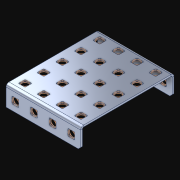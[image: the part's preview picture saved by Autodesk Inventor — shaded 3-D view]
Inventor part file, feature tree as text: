
AUTODESK INVENTOR PART (.ipt)
format: ipt  version: 2021 (Build 250183000, 183)  size: 1,430,528 bytes
history: native  units: in
note: dims shown in document units (in); Inventor stores cm internally (conversion verified against a paired STEP export)
features: extrude x29, other x29, sketch x4, pattern_linear x3
ambient origin geometry x8: Origin, YZ Plane, XZ Plane, XY Plane, X Axis, Y Axis, Z Axis, Center Point
bodies: Solid1 (feature_tree)
feature tree (65):
  pattern_linear  "Rectangular Pattern1"  Spacing1=0.182in  [1 undecoded]
  pattern_linear  "Rectangular Pattern2"  Spacing1=0.046in  [1 undecoded]
  pattern_linear  "Rectangular Pattern3"  Spacing1=0.5in  [1 undecoded]
  extrude  "Extrusion1"  Depth=0.5in
  sketch  "Sketch1"  dims[d0=0.182in]
  other  "Srf1"
  sketch  "Sketch2"  dims[d1=0.046in d2=0.0in]
  other  "Srf2"
  sketch  "Sketch3"  dims[d3=0.182in]
  other  "Srf3"
  other  "Srf4"
  other  "Srf5"
  other  "Srf6"
  other  "Srf38"
  other  "Srf39"
  other  "Srf40"
  other  "Srf72"
  other  "Srf73"
  other  "Srf74"
  other  "Srf75"
  other  "Srf107"
  other  "Srf108"
  other  "Srf109"
  other  "Srf110"
  other  "Srf142"
  other  "Srf143"
  other  "Srf144"
  other  "Srf145"
  other  "Srf177"
  other  "Srf178"
  other  "Srf179"
  other  "Srf180"
  other  "Srf212"
  other  "Srf213"
  other  "Srf214"
  sketch  "Sketch4"  dims[d4=0.046in d5=0.0in d6=0.182in d7=0.046in d8=0.0in d11=0.5in d12=1.5748in d14=0.5in d15=1.9685in d17=0.5in d18=1.5748in d20=0.5in d21=15.5in d22=0.0in]
  parser-record x1  (decoder bookkeeping rows leaked as tree rows — omitted from the tree; the rows remain in map.json)
  extrude  "ExtrusionSrf1"  Depth=0.5in
  extrude  "ExtrusionSrf2"  Depth=0.5in
  extrude  "ExtrusionSrf3"  Depth=0.5in
  extrude  "ExtrusionSrf4"  Depth=0.5in
  extrude  "ExtrusionSrf5"  Depth=0.5in
  extrude  "ExtrusionSrf6"  TaperAngle=0.0deg  [1 undecoded]
  extrude  "ExtrusionSrf38"  [1 undecoded]
  extrude  "ExtrusionSrf39"  [1 undecoded]
  extrude  "ExtrusionSrf40"  [1 undecoded]
  extrude  "ExtrusionSrf72"  [1 undecoded]
  extrude  "ExtrusionSrf73"  [1 undecoded]
  extrude  "ExtrusionSrf74"  [1 undecoded]
  extrude  "ExtrusionSrf75"  [1 undecoded]
  extrude  "ExtrusionSrf107"  [1 undecoded]
  extrude  "ExtrusionSrf108"  [1 undecoded]
  extrude  "ExtrusionSrf109"  [1 undecoded]
  extrude  "ExtrusionSrf110"  [1 undecoded]
  extrude  "ExtrusionSrf142"  [1 undecoded]
  extrude  "ExtrusionSrf143"  [1 undecoded]
  extrude  "ExtrusionSrf144"  [1 undecoded]
  extrude  "ExtrusionSrf145"  [1 undecoded]
  extrude  "ExtrusionSrf177"  [1 undecoded]
  extrude  "ExtrusionSrf178"  [1 undecoded]
  extrude  "ExtrusionSrf179"  [1 undecoded]
  extrude  "ExtrusionSrf180"  [1 undecoded]
  extrude  "ExtrusionSrf212"  [1 undecoded]
  extrude  "ExtrusionSrf213"  [1 undecoded]
  extrude  "ExtrusionSrf214"  [1 undecoded]
note: 26 required parameter values undecoded (feature->parameter linkage not recoverable at this tier; creation-order binding heuristic only, values carry confidence <= 0.55)
